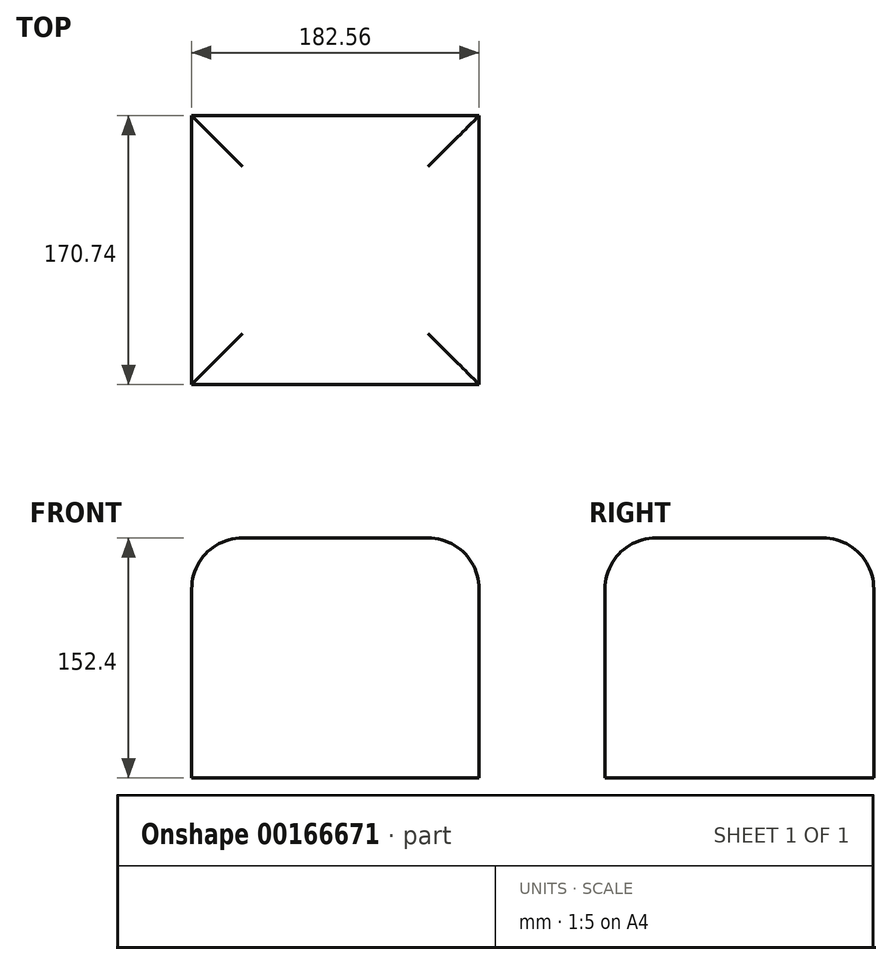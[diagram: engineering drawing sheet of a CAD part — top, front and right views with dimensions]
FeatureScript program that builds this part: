
annotation { "Feature Type Name" : "Feature", "Feature Type Description" : "" }
export const myFeature = defineFeature(function(context is Context, id is Id, definition is map)
    precondition{}
    {
        {
            var Q0;
            Q0=qCreatedBy(makeId("Top.planeOp"),FACE);
            var sketch = newSketch(context, id + "F0", { "sketchPlane" : qUnion([Q0])});
            skLineSegment(sketch, "E0.bottom", {"start": v(47.67, -43.6) * mm, "end": v(-134.89, -43.6) * mm});
            skLineSegment(sketch, "E0.top", {"start": v(47.67, 127.13) * mm, "end": v(-134.89, 127.13) * mm});
            skLineSegment(sketch, "E0.left", {"start": v(47.67, -43.6) * mm, "end": v(47.67, 127.13) * mm});
            skLineSegment(sketch, "E0.right", {"start": v(-134.89, -43.6) * mm, "end": v(-134.89, 127.13) * mm});
            skPoint(sketch, "E0.middle", {"position": v(-43.6, 41.76) * mm});
            skSolve(sketch);
        }
        {
            var Q0;
            Q0=makeQuery(id+"F0.imprint","IMPRINT",FACE,{"disambiguationData":[TD([[makeQuery(id+"F0.imprint","IMPRINT",EDGE,{"derivedFrom":sQuery(id+"F0.wireOp",EDGE,"E0.bottom")}),-1.0]])]});
            var sketch = newSketch(context, id + "F1", { "sketchPlane" : qUnion([Q0])});
            skLineSegment(sketch, "E1.bottom", {"start": v(0, 80.7) * mm, "end": v(-209.9, 80.7) * mm});
            skLineSegment(sketch, "E1.top", {"start": v(0, -80.7) * mm, "end": v(-209.9, -80.7) * mm});
            skLineSegment(sketch, "E1.left", {"start": v(0, 80.7) * mm, "end": v(0, -80.7) * mm});
            skLineSegment(sketch, "E1.right", {"start": v(-209.9, 80.7) * mm, "end": v(-209.9, -80.7) * mm});
            skPoint(sketch, "E1.middle", {"position": v(-104.95, 0) * mm});
            skSolve(sketch);
        }
        {
            var Q0;
            Q0 = qSketchRegion(id + "F0", true);
            extrude(context, id + "F2", {"entities" : qUnion([Q0]), "depth" : 152.4 * mm});
        }
        {
            var Q0;
            Q0=makeQuery(id+"F2.opExtrude","CAP_EDGE",EDGE,{"disambiguationData":[OSD([sQuery(id+"F0.wireOp",EDGE,"E0.top")])],"isStart":false});
            var Q1;
            Q1=makeQuery(id+"F2.opExtrude","CAP_EDGE",EDGE,{"disambiguationData":[OSD([sQuery(id+"F0.wireOp",EDGE,"E0.left")])],"isStart":false});
            var Q2;
            Q2=makeQuery(id+"F2.opExtrude","CAP_EDGE",EDGE,{"disambiguationData":[OSD([sQuery(id+"F0.wireOp",EDGE,"E0.bottom")])],"isStart":false});
            var Q3;
            Q3=makeQuery(id+"F2.opExtrude","CAP_EDGE",EDGE,{"disambiguationData":[OSD([sQuery(id+"F0.wireOp",EDGE,"E0.right")])],"isStart":false});
            fillet(context, id + "F3", {"entities" : qUnion([Q0, Q1, Q2, Q3]), "radius" : 32.27 * mm, "tangentPropagation" : true, "allowEdgeOverflow" : false});
        }
        {
            var Q0;
            {var subQ1=sQuery(id+"F1.wireOp",EDGE,"E1.top");Q0=makeQuery(id+"F1.imprint","IMPRINT",FACE,{"disambiguationData":[TD([[makeQuery(id+"F1.imprint","IMPRINT",EDGE,{"derivedFrom":subQ1}),-1.0]])]});}
            extrude(context, id + "F4", {"entities" : qUnion([Q0]), "operationType" : NewBodyOperationType.REMOVE, "depth" : 187.38 * mm});
        }
    });
